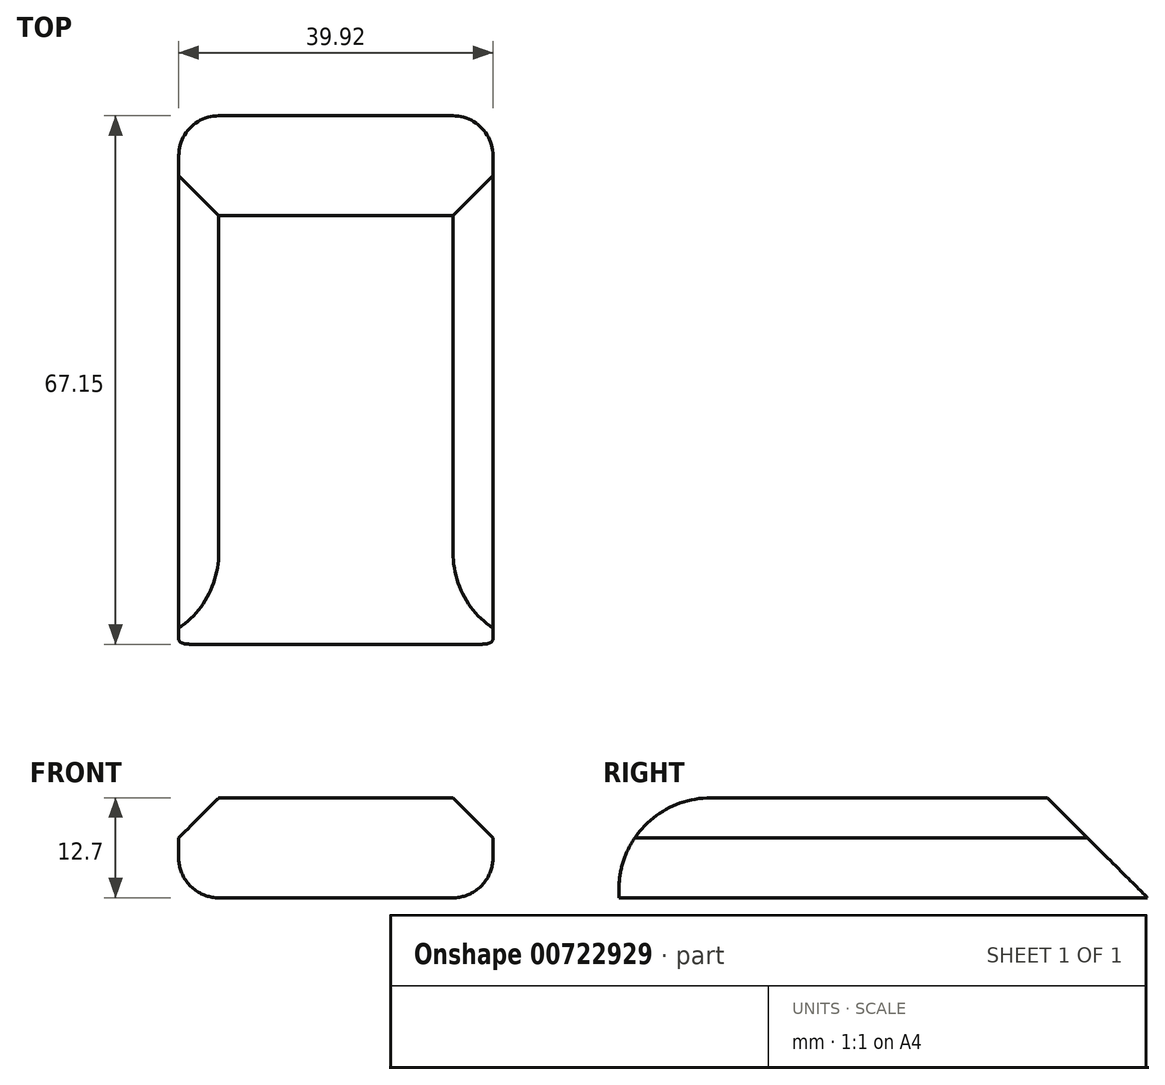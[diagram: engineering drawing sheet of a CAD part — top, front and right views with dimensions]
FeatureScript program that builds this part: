
annotation { "Feature Type Name" : "Feature", "Feature Type Description" : "" }
export const myFeature = defineFeature(function(context is Context, id is Id, definition is map)
    precondition{}
    {
        {
            var Q0;
            Q0=qCreatedBy(makeId("Top.planeOp"),FACE);
            var sketch = newSketch(context, id + "F0", { "sketchPlane" : qUnion([Q0])});
            skLineSegment(sketch, "E0", {"start": v(19.96, 33.01) * mm, "end": v(19.96, -46.84) * mm});
            skLineSegment(sketch, "E1.MirrorCS", {"start": v(-19.96, 33.01) * mm, "end": v(-19.96, -46.84) * mm});
            skLineSegment(sketch, "E2", {"start": v(-19.96, 33.01) * mm, "end": v(19.96, 33.01) * mm});
            skLineSegment(sketch, "E3", {"start": v(-19.96, -46.84) * mm, "end": v(19.96, -46.84) * mm});
            skSolve(sketch);
        }
        {
            var Q0;
            Q0=makeQuery(id+"F0.imprint","IMPRINT",FACE,{"disambiguationData":[TD([[makeQuery(id+"F0.imprint","IMPRINT",EDGE,{"derivedFrom":sQuery(id+"F0.wireOp",EDGE,"E0")}),-1.0]])]});
            extrude(context, id + "F1", {"entities" : qUnion([Q0]), "depth" : 12.7 * mm, "offsetDistance" : 25.4 * mm});
        }
        {
            var Q0;
            Q0=makeQuery(id+"F1.opExtrude","CAP_EDGE",EDGE,{"disambiguationData":[OSD([sQuery(id+"F0.wireOp",EDGE,"E2")])],"isStart":false});
            chamfer(context, id + "F2", {"entities" : qUnion([Q0]), "width" : 25.4 * mm, "tangentPropagation" : true});
        }
        {
            var Q0;
            Q0=makeQuery(id+"F1.opExtrude","CAP_EDGE",EDGE,{"disambiguationData":[OSD([sQuery(id+"F0.wireOp",EDGE,"E0")])],"isStart":true});
            var Q1;
            Q1=makeQuery(id+"F1.opExtrude","CAP_EDGE",EDGE,{"disambiguationData":[OSD([sQuery(id+"F0.wireOp",EDGE,"E1.MirrorCS")])],"isStart":true});
            fillet(context, id + "F3", {"entities" : qUnion([Q0, Q1]), "radius" : 5.08 * mm, "tangentPropagation" : true, "allowEdgeOverflow" : false});
        }
        {
            var Q0;
            Q0=makeQuery(id+"F1.opExtrude","CAP_EDGE",EDGE,{"disambiguationData":[OSD([sQuery(id+"F0.wireOp",EDGE,"E1.MirrorCS")])],"isStart":false});
            var Q1;
            Q1=makeQuery(id+"F1.opExtrude","CAP_EDGE",EDGE,{"disambiguationData":[OSD([sQuery(id+"F0.wireOp",EDGE,"E0")])],"isStart":false});
            chamfer(context, id + "F4", {"entities" : qUnion([Q0, Q1]), "width" : 5.08 * mm, "tangentPropagation" : true});
        }
        {
            var Q0;
            Q0=makeQuery(id+"F1.opExtrude","CAP_EDGE",EDGE,{"disambiguationData":[OSD([sQuery(id+"F0.wireOp",EDGE,"E3")])],"isStart":false});
            fillet(context, id + "F5", {"entities" : qUnion([Q0]), "radius" : 11.65 * mm, "tangentPropagation" : true, "allowEdgeOverflow" : false});
        }
    });
